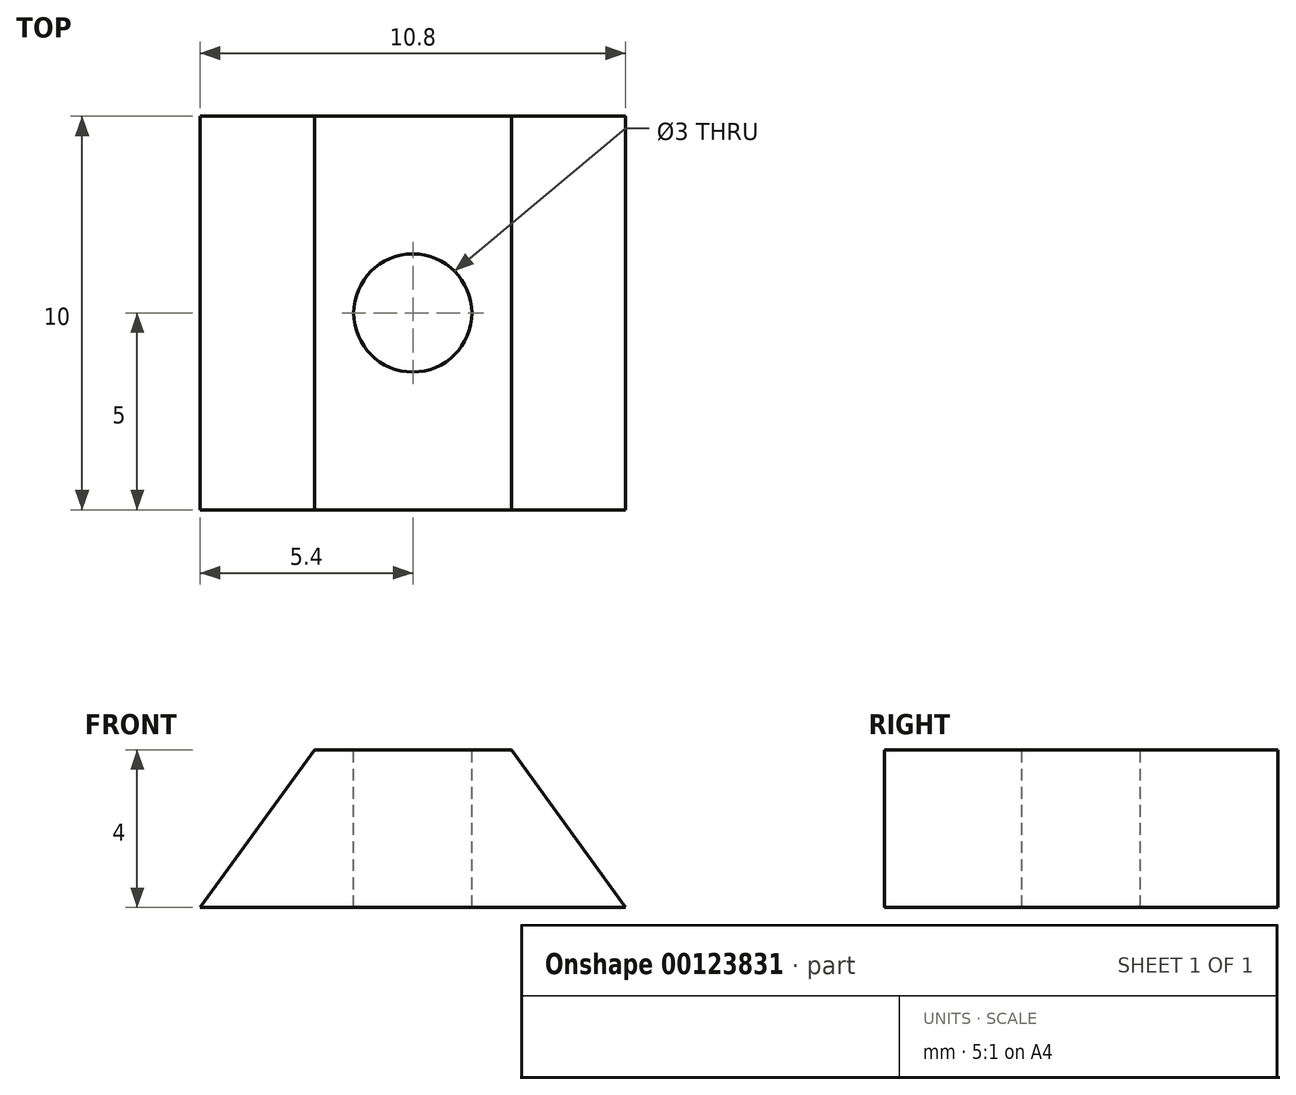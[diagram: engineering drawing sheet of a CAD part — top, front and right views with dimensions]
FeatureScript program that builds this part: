
annotation { "Feature Type Name" : "Feature", "Feature Type Description" : "" }
export const myFeature = defineFeature(function(context is Context, id is Id, definition is map)
    precondition{}
    {
        {
            var Q0;
            Q0=qCreatedBy(makeId("Front.planeOp"),FACE);
            var sketch = newSketch(context, id + "F0", { "sketchPlane" : qUnion([Q0])});
            skLineSegment(sketch, "E0", {"start": v(-5.4, 0) * mm, "end": v(5.4, 0) * mm});
            skLineSegment(sketch, "E1", {"start": v(5.4, 0) * mm, "end": v(2.5, 4) * mm});
            skLineSegment(sketch, "E2", {"start": v(2.5, 4) * mm, "end": v(-2.5, 4) * mm});
            skLineSegment(sketch, "E3", {"start": v(-2.5, 4) * mm, "end": v(-5.4, 0) * mm});
            skSolve(sketch);
        }
        {
            var Q0;
            Q0=makeQuery(id+"F0.imprint","IMPRINT",FACE,{"disambiguationData":[TD([[makeQuery(id+"F0.imprint","IMPRINT",EDGE,{"derivedFrom":sQuery(id+"F0.wireOp",EDGE,"E0")}),1.0]])]});
            extrude(context, id + "F1", {"entities" : qUnion([Q0]), "depth" : 10 * mm});
        }
        {
            var Q0;
            Q0=makeQuery(id+"F1.opExtrude","SWEPT_FACE",FACE,{"disambiguationData":[OSD([sQuery(id+"F0.wireOp",EDGE,"E2")])]});
            var sketch = newSketch(context, id + "F2", { "sketchPlane" : qUnion([Q0])});
            skLineSegment(sketch, "E4", {"start": v(-7.26, -5) * mm, "end": v(7.26, -5) * mm, "construction": true});
            skCircle(sketch, "E5", {"center": v(0, -5) * mm, "radius": 1.5 * mm});
            skPoint(sketch, "E5.centerSnap0", {"position": v(0, -5) * mm});
            skSolve(sketch);
        }
        {
            var Q0;
            Q0=makeQuery(id+"F2.imprint","IMPRINT",FACE,{"disambiguationData":[TD([[makeQuery(id+"F2.imprint","IMPRINT",EDGE,{"derivedFrom":sQuery(id+"F2.wireOp",EDGE,"E5")}),1.0]])]});
            extrude(context, id + "F3", {"entities" : qUnion([Q0]), "operationType" : NewBodyOperationType.REMOVE, "oppositeDirection" : true, "depth" : 5 * mm});
        }
    });
